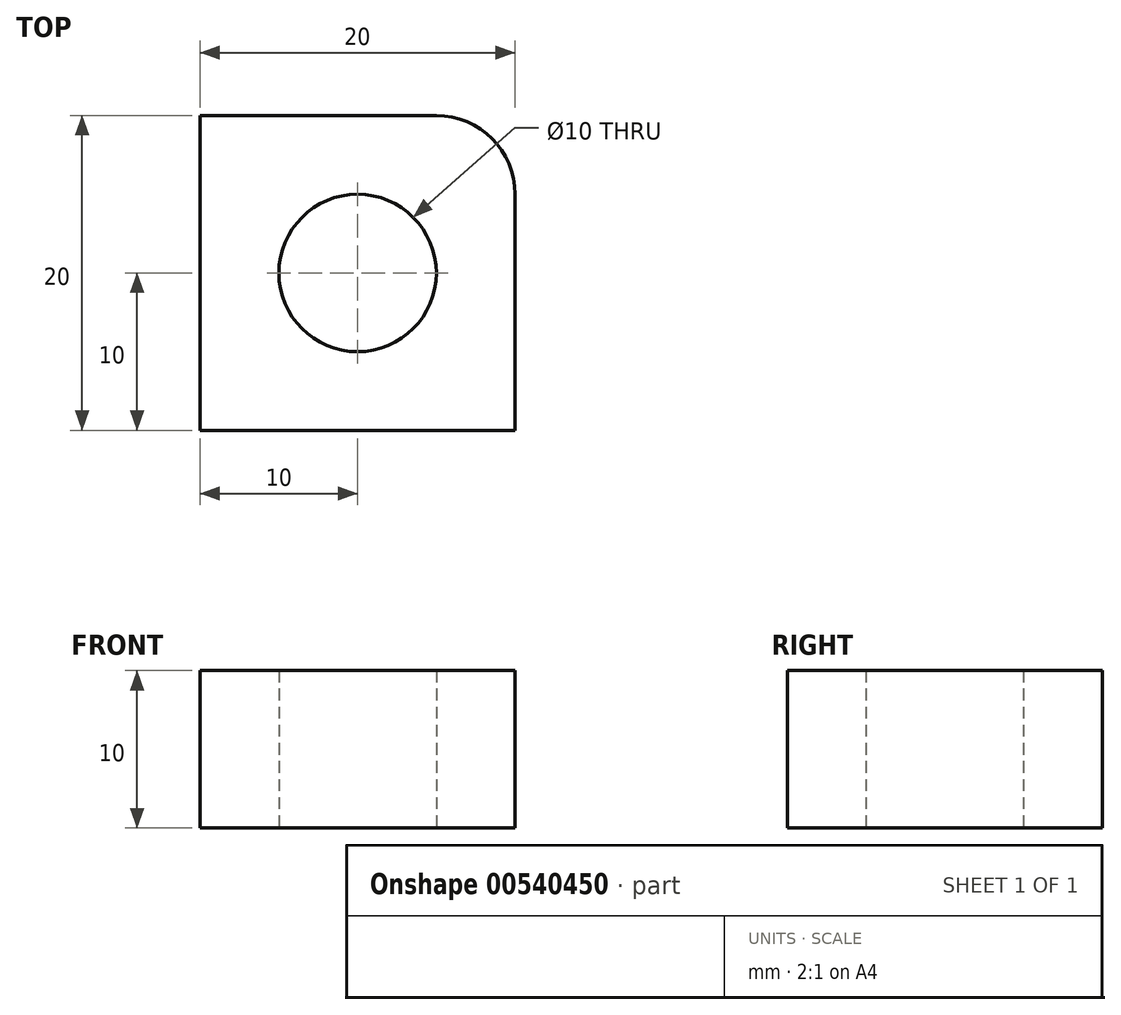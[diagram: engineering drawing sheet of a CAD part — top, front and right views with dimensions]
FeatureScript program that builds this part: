
annotation { "Feature Type Name" : "Feature", "Feature Type Description" : "" }
export const myFeature = defineFeature(function(context is Context, id is Id, definition is map)
    precondition{}
    {
        {
            var Q0;
            Q0=qCreatedBy(makeId("Top.planeOp"),FACE);
            var sketch = newSketch(context, id + "F0", { "sketchPlane" : qUnion([Q0])});
            skLineSegment(sketch, "E0.bottom", {"start": v(10, -10) * mm, "end": v(-10, -10) * mm});
            skLineSegment(sketch, "E0.top", {"start": v(5, 10) * mm, "end": v(-10, 10) * mm});
            skLineSegment(sketch, "E0.left", {"start": v(10, -10) * mm, "end": v(10, 5) * mm});
            skLineSegment(sketch, "E0.right", {"start": v(-10, -10) * mm, "end": v(-10, 10) * mm});
            skPoint(sketch, "E0.middle", {"position": v(0, 0) * mm});
            skPoint(sketch, "E1.visualSharp", {"position": v(10, 10) * mm});
            skArc(sketch, "E1.filletArc", {"start": v(10, 5) * mm, "mid": v(8.54, 8.54) * mm, "end": v(5, 10) * mm});
            skCircle(sketch, "E2", {"center": v(0, 0) * mm, "radius": 5 * mm});
            skSolve(sketch);
        }
        {
            var Q0;
            Q0 = qSketchRegion(id + "F0", true);
            extrude(context, id + "F1", {"entities" : qUnion([Q0]), "depth" : 10 * mm, "offsetDistance" : 25 * mm});
        }
    });
